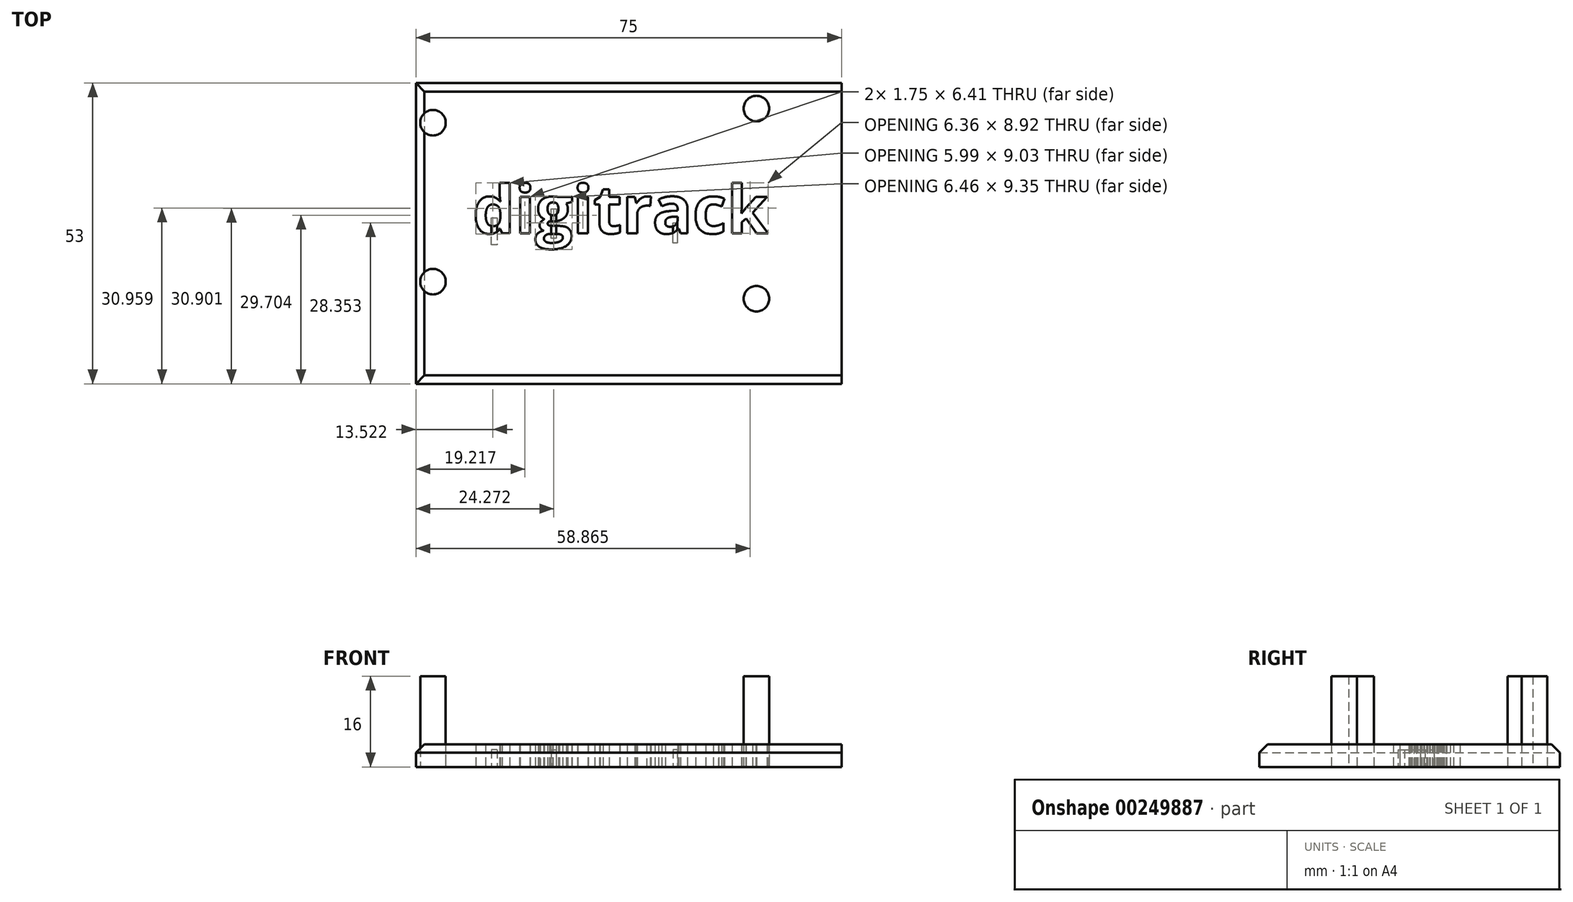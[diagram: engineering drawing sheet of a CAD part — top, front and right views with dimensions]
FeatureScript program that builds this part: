
annotation { "Feature Type Name" : "Feature", "Feature Type Description" : "" }
export const myFeature = defineFeature(function(context is Context, id is Id, definition is map)
    precondition{}
    {
        {
            var Q0;
            Q0=qCreatedBy(makeId("Top.planeOp"),FACE);
            var sketch = newSketch(context, id + "F0", { "sketchPlane" : qUnion([Q0])});
            skLineSegment(sketch, "E0.bottom", {"start": v(37.5, -26.5) * mm, "end": v(-37.5, -26.5) * mm});
            skLineSegment(sketch, "E0.top", {"start": v(37.5, 26.5) * mm, "end": v(-37.5, 26.5) * mm});
            skLineSegment(sketch, "E0.left", {"start": v(37.5, -26.5) * mm, "end": v(37.5, 26.5) * mm});
            skLineSegment(sketch, "E0.right", {"start": v(-37.5, -26.5) * mm, "end": v(-37.5, 26.5) * mm});
            skPoint(sketch, "E0.middle", {"position": v(0, 0) * mm});
            skSolve(sketch);
        }
        {
            var Q0;
            Q0 = qSketchRegion(id + "F0", true);
            extrude(context, id + "F1", {"entities" : qUnion([Q0]), "depth" : 4 * mm});
        }
        {
            var Q0;
            Q0=qCreatedBy(makeId("Top.planeOp"),FACE);
            var sketch = newSketch(context, id + "F2", { "sketchPlane" : qUnion([Q0])});
            skLineSegment(sketch, "E1", {"start": v(0, 0) * mm, "end": v(37.5, 0) * mm});
            skLineSegment(sketch, "E2", {"start": v(37.5, 0) * mm, "end": v(22.5, 0) * mm});
            skLineSegment(sketch, "E3", {"start": v(22.5, 0) * mm, "end": v(22.5, 22) * mm});
            skLineSegment(sketch, "E4", {"start": v(22.5, 0) * mm, "end": v(22.5, -26.5) * mm});
            skLineSegment(sketch, "E5", {"start": v(22.5, -26.5) * mm, "end": v(22.5, -11.5) * mm});
            skLineSegment(sketch, "E6", {"start": v(0, 0) * mm, "end": v(-37.5, 0) * mm});
            skLineSegment(sketch, "E7", {"start": v(-37.5, 0) * mm, "end": v(-34.5, 0) * mm});
            skLineSegment(sketch, "E8", {"start": v(-34.5, 0) * mm, "end": v(-34.5, 26.5) * mm});
            skLineSegment(sketch, "E9", {"start": v(-34.5, 26.5) * mm, "end": v(-34.5, 19.5) * mm});
            skLineSegment(sketch, "E10", {"start": v(-34.5, 0) * mm, "end": v(-34.5, -26.5) * mm});
            skLineSegment(sketch, "E11", {"start": v(-34.5, -26.5) * mm, "end": v(-34.5, -8.5) * mm});
            skCircle(sketch, "E12", {"center": v(-34.5, -8.5) * mm, "radius": 2.25 * mm});
            skCircle(sketch, "E13", {"center": v(-34.5, 19.5) * mm, "radius": 2.25 * mm});
            skCircle(sketch, "E14", {"center": v(22.5, 22) * mm, "radius": 2.25 * mm});
            skCircle(sketch, "E15", {"center": v(22.5, -11.5) * mm, "radius": 2.25 * mm});
            skSolve(sketch);
        }
        {
            var Q0;
            Q0 = qSketchRegion(id + "F2", true);
            extrude(context, id + "F3", {"entities" : qUnion([Q0]), "depth" : 16 * mm});
        }
        {
            var Q0;
            Q0=makeQuery(id+"F1.opExtrude","CAP_EDGE",EDGE,{"disambiguationData":[OSD([sQuery(id+"F0.wireOp",EDGE,"E0.right")])],"isStart":false});
            var Q1;
            Q1=makeQuery(id+"F1.opExtrude","CAP_EDGE",EDGE,{"disambiguationData":[OSD([sQuery(id+"F0.wireOp",EDGE,"E0.bottom")])],"isStart":false});
            var Q2;
            Q2=makeQuery(id+"F1.opExtrude","CAP_EDGE",EDGE,{"disambiguationData":[OSD([sQuery(id+"F0.wireOp",EDGE,"E0.top")])],"isStart":false});
            chamfer(context, id + "F4", {"entities" : qUnion([Q0, Q1, Q2]), "width" : 1.5 * mm, "tangentPropagation" : true});
        }
        {
            var Q0;
            Q0=qCreatedBy(makeId("Top.planeOp"),FACE);
            var sketch = newSketch(context, id + "F5", { "sketchPlane" : qUnion([Q0])});
            skText(sketch, "E16", { "text": "digitrack", "fontName": "OpenSans-Bold.ttf"});
            const initialGuessF5  = {"E16": [0, 0, 1, 0, 0.00845]};
            skSetInitialGuess(sketch, initialGuessF5);
            skSolve(sketch);
        }
        {
            var Q0;
            Q0 = qSketchRegion(id + "F5", true);
            extrude(context, id + "F6", {"entities" : qUnion([Q0]), "depth" : 8 * mm});
        }
        {
            var Q0;
            Q0=makeQuery(id+"F6.opExtrude","SWEPT_BODY",BODY,{"disambiguationData":[OSD([sQuery(id+"F5.wireOp",EDGE,"E16.sketch_text.stroke-0"),sQuery(id+"F5.wireOp",EDGE,"E16.sketch_text.stroke-1"),sQuery(id+"F5.wireOp",EDGE,"E16.sketch_text.stroke-2"),sQuery(id+"F5.wireOp",EDGE,"E16.sketch_text.stroke-3"),sQuery(id+"F5.wireOp",EDGE,"E16.sketch_text.stroke-4"),sQuery(id+"F5.wireOp",EDGE,"E16.sketch_text.stroke-5"),sQuery(id+"F5.wireOp",EDGE,"E16.sketch_text.stroke-6"),sQuery(id+"F5.wireOp",EDGE,"E16.sketch_text.stroke-7"),sQuery(id+"F5.wireOp",EDGE,"E16.sketch_text.stroke-8"),sQuery(id+"F5.wireOp",EDGE,"E16.sketch_text.stroke-9"),sQuery(id+"F5.wireOp",EDGE,"E16.sketch_text.stroke-10"),sQuery(id+"F5.wireOp",EDGE,"E16.sketch_text.stroke-11"),sQuery(id+"F5.wireOp",EDGE,"E16.sketch_text.stroke-12"),sQuery(id+"F5.wireOp",EDGE,"E16.sketch_text.stroke-13"),sQuery(id+"F5.wireOp",EDGE,"E16.sketch_text.stroke-14"),sQuery(id+"F5.wireOp",EDGE,"E16.sketch_text.stroke-15"),sQuery(id+"F5.wireOp",EDGE,"E16.sketch_text.stroke-16"),sQuery(id+"F5.wireOp",EDGE,"E16.sketch_text.stroke-17"),sQuery(id+"F5.wireOp",EDGE,"E16.sketch_text.stroke-18"),sQuery(id+"F5.wireOp",EDGE,"E16.sketch_text.stroke-19"),sQuery(id+"F5.wireOp",EDGE,"E16.sketch_text.stroke-20"),sQuery(id+"F5.wireOp",EDGE,"E16.sketch_text.stroke-21"),sQuery(id+"F5.wireOp",EDGE,"E16.sketch_text.stroke-22")])]});
            var Q1;
            Q1=makeQuery(id+"F6.opExtrude","SWEPT_BODY",BODY,{"disambiguationData":[OSD([sQuery(id+"F5.wireOp",EDGE,"E16.sketch_text.stroke-23"),sQuery(id+"F5.wireOp",EDGE,"E16.sketch_text.stroke-24"),sQuery(id+"F5.wireOp",EDGE,"E16.sketch_text.stroke-25"),sQuery(id+"F5.wireOp",EDGE,"E16.sketch_text.stroke-26"),sQuery(id+"F5.wireOp",EDGE,"E16.sketch_text.stroke-27")])]});
            var Q2;
            Q2=makeQuery(id+"F6.opExtrude","SWEPT_BODY",BODY,{"disambiguationData":[OSD([sQuery(id+"F5.wireOp",EDGE,"E16.sketch_text.stroke-28"),sQuery(id+"F5.wireOp",EDGE,"E16.sketch_text.stroke-29"),sQuery(id+"F5.wireOp",EDGE,"E16.sketch_text.stroke-30"),sQuery(id+"F5.wireOp",EDGE,"E16.sketch_text.stroke-31")])]});
            var Q3;
            Q3=makeQuery(id+"F6.opExtrude","SWEPT_BODY",BODY,{"disambiguationData":[OSD([sQuery(id+"F5.wireOp",EDGE,"E16.sketch_text.stroke-32"),sQuery(id+"F5.wireOp",EDGE,"E16.sketch_text.stroke-33"),sQuery(id+"F5.wireOp",EDGE,"E16.sketch_text.stroke-34"),sQuery(id+"F5.wireOp",EDGE,"E16.sketch_text.stroke-35"),sQuery(id+"F5.wireOp",EDGE,"E16.sketch_text.stroke-36"),sQuery(id+"F5.wireOp",EDGE,"E16.sketch_text.stroke-37"),sQuery(id+"F5.wireOp",EDGE,"E16.sketch_text.stroke-38"),sQuery(id+"F5.wireOp",EDGE,"E16.sketch_text.stroke-39"),sQuery(id+"F5.wireOp",EDGE,"E16.sketch_text.stroke-40"),sQuery(id+"F5.wireOp",EDGE,"E16.sketch_text.stroke-41"),sQuery(id+"F5.wireOp",EDGE,"E16.sketch_text.stroke-42"),sQuery(id+"F5.wireOp",EDGE,"E16.sketch_text.stroke-43"),sQuery(id+"F5.wireOp",EDGE,"E16.sketch_text.stroke-44"),sQuery(id+"F5.wireOp",EDGE,"E16.sketch_text.stroke-45"),sQuery(id+"F5.wireOp",EDGE,"E16.sketch_text.stroke-46"),sQuery(id+"F5.wireOp",EDGE,"E16.sketch_text.stroke-47"),sQuery(id+"F5.wireOp",EDGE,"E16.sketch_text.stroke-48"),sQuery(id+"F5.wireOp",EDGE,"E16.sketch_text.stroke-49"),sQuery(id+"F5.wireOp",EDGE,"E16.sketch_text.stroke-50"),sQuery(id+"F5.wireOp",EDGE,"E16.sketch_text.stroke-51"),sQuery(id+"F5.wireOp",EDGE,"E16.sketch_text.stroke-52"),sQuery(id+"F5.wireOp",EDGE,"E16.sketch_text.stroke-53"),sQuery(id+"F5.wireOp",EDGE,"E16.sketch_text.stroke-54"),sQuery(id+"F5.wireOp",EDGE,"E16.sketch_text.stroke-55"),sQuery(id+"F5.wireOp",EDGE,"E16.sketch_text.stroke-56"),sQuery(id+"F5.wireOp",EDGE,"E16.sketch_text.stroke-57"),sQuery(id+"F5.wireOp",EDGE,"E16.sketch_text.stroke-58"),sQuery(id+"F5.wireOp",EDGE,"E16.sketch_text.stroke-59"),sQuery(id+"F5.wireOp",EDGE,"E16.sketch_text.stroke-60"),sQuery(id+"F5.wireOp",EDGE,"E16.sketch_text.stroke-61"),sQuery(id+"F5.wireOp",EDGE,"E16.sketch_text.stroke-62"),sQuery(id+"F5.wireOp",EDGE,"E16.sketch_text.stroke-63"),sQuery(id+"F5.wireOp",EDGE,"E16.sketch_text.stroke-64"),sQuery(id+"F5.wireOp",EDGE,"E16.sketch_text.stroke-65"),sQuery(id+"F5.wireOp",EDGE,"E16.sketch_text.stroke-66"),sQuery(id+"F5.wireOp",EDGE,"E16.sketch_text.stroke-67"),sQuery(id+"F5.wireOp",EDGE,"E16.sketch_text.stroke-68"),sQuery(id+"F5.wireOp",EDGE,"E16.sketch_text.stroke-69"),sQuery(id+"F5.wireOp",EDGE,"E16.sketch_text.stroke-70"),sQuery(id+"F5.wireOp",EDGE,"E16.sketch_text.stroke-71"),sQuery(id+"F5.wireOp",EDGE,"E16.sketch_text.stroke-72"),sQuery(id+"F5.wireOp",EDGE,"E16.sketch_text.stroke-73"),sQuery(id+"F5.wireOp",EDGE,"E16.sketch_text.stroke-74"),sQuery(id+"F5.wireOp",EDGE,"E16.sketch_text.stroke-75")])]});
            var Q4;
            Q4=makeQuery(id+"F6.opExtrude","SWEPT_BODY",BODY,{"disambiguationData":[OSD([sQuery(id+"F5.wireOp",EDGE,"E16.sketch_text.stroke-76"),sQuery(id+"F5.wireOp",EDGE,"E16.sketch_text.stroke-77"),sQuery(id+"F5.wireOp",EDGE,"E16.sketch_text.stroke-78"),sQuery(id+"F5.wireOp",EDGE,"E16.sketch_text.stroke-79"),sQuery(id+"F5.wireOp",EDGE,"E16.sketch_text.stroke-80")])]});
            var Q5;
            Q5=makeQuery(id+"F6.opExtrude","SWEPT_BODY",BODY,{"disambiguationData":[OSD([sQuery(id+"F5.wireOp",EDGE,"E16.sketch_text.stroke-81"),sQuery(id+"F5.wireOp",EDGE,"E16.sketch_text.stroke-82"),sQuery(id+"F5.wireOp",EDGE,"E16.sketch_text.stroke-83"),sQuery(id+"F5.wireOp",EDGE,"E16.sketch_text.stroke-84")])]});
            var Q6;
            Q6=makeQuery(id+"F6.opExtrude","SWEPT_BODY",BODY,{"disambiguationData":[OSD([sQuery(id+"F5.wireOp",EDGE,"E16.sketch_text.stroke-85"),sQuery(id+"F5.wireOp",EDGE,"E16.sketch_text.stroke-86"),sQuery(id+"F5.wireOp",EDGE,"E16.sketch_text.stroke-87"),sQuery(id+"F5.wireOp",EDGE,"E16.sketch_text.stroke-88"),sQuery(id+"F5.wireOp",EDGE,"E16.sketch_text.stroke-89"),sQuery(id+"F5.wireOp",EDGE,"E16.sketch_text.stroke-90"),sQuery(id+"F5.wireOp",EDGE,"E16.sketch_text.stroke-91"),sQuery(id+"F5.wireOp",EDGE,"E16.sketch_text.stroke-92"),sQuery(id+"F5.wireOp",EDGE,"E16.sketch_text.stroke-93"),sQuery(id+"F5.wireOp",EDGE,"E16.sketch_text.stroke-94"),sQuery(id+"F5.wireOp",EDGE,"E16.sketch_text.stroke-95"),sQuery(id+"F5.wireOp",EDGE,"E16.sketch_text.stroke-96"),sQuery(id+"F5.wireOp",EDGE,"E16.sketch_text.stroke-97"),sQuery(id+"F5.wireOp",EDGE,"E16.sketch_text.stroke-98"),sQuery(id+"F5.wireOp",EDGE,"E16.sketch_text.stroke-99"),sQuery(id+"F5.wireOp",EDGE,"E16.sketch_text.stroke-100"),sQuery(id+"F5.wireOp",EDGE,"E16.sketch_text.stroke-101"),sQuery(id+"F5.wireOp",EDGE,"E16.sketch_text.stroke-102")])]});
            var Q7;
            Q7=makeQuery(id+"F6.opExtrude","SWEPT_BODY",BODY,{"disambiguationData":[OSD([sQuery(id+"F5.wireOp",EDGE,"E16.sketch_text.stroke-103"),sQuery(id+"F5.wireOp",EDGE,"E16.sketch_text.stroke-104"),sQuery(id+"F5.wireOp",EDGE,"E16.sketch_text.stroke-105"),sQuery(id+"F5.wireOp",EDGE,"E16.sketch_text.stroke-106"),sQuery(id+"F5.wireOp",EDGE,"E16.sketch_text.stroke-107"),sQuery(id+"F5.wireOp",EDGE,"E16.sketch_text.stroke-108"),sQuery(id+"F5.wireOp",EDGE,"E16.sketch_text.stroke-109"),sQuery(id+"F5.wireOp",EDGE,"E16.sketch_text.stroke-110"),sQuery(id+"F5.wireOp",EDGE,"E16.sketch_text.stroke-111"),sQuery(id+"F5.wireOp",EDGE,"E16.sketch_text.stroke-112"),sQuery(id+"F5.wireOp",EDGE,"E16.sketch_text.stroke-113"),sQuery(id+"F5.wireOp",EDGE,"E16.sketch_text.stroke-114"),sQuery(id+"F5.wireOp",EDGE,"E16.sketch_text.stroke-115")])]});
            var Q8;
            Q8=makeQuery(id+"F6.opExtrude","SWEPT_BODY",BODY,{"disambiguationData":[OSD([sQuery(id+"F5.wireOp",EDGE,"E16.sketch_text.stroke-116"),sQuery(id+"F5.wireOp",EDGE,"E16.sketch_text.stroke-117"),sQuery(id+"F5.wireOp",EDGE,"E16.sketch_text.stroke-118"),sQuery(id+"F5.wireOp",EDGE,"E16.sketch_text.stroke-119"),sQuery(id+"F5.wireOp",EDGE,"E16.sketch_text.stroke-120"),sQuery(id+"F5.wireOp",EDGE,"E16.sketch_text.stroke-121"),sQuery(id+"F5.wireOp",EDGE,"E16.sketch_text.stroke-122"),sQuery(id+"F5.wireOp",EDGE,"E16.sketch_text.stroke-123"),sQuery(id+"F5.wireOp",EDGE,"E16.sketch_text.stroke-124"),sQuery(id+"F5.wireOp",EDGE,"E16.sketch_text.stroke-125"),sQuery(id+"F5.wireOp",EDGE,"E16.sketch_text.stroke-126"),sQuery(id+"F5.wireOp",EDGE,"E16.sketch_text.stroke-127"),sQuery(id+"F5.wireOp",EDGE,"E16.sketch_text.stroke-128"),sQuery(id+"F5.wireOp",EDGE,"E16.sketch_text.stroke-129"),sQuery(id+"F5.wireOp",EDGE,"E16.sketch_text.stroke-130"),sQuery(id+"F5.wireOp",EDGE,"E16.sketch_text.stroke-131"),sQuery(id+"F5.wireOp",EDGE,"E16.sketch_text.stroke-132"),sQuery(id+"F5.wireOp",EDGE,"E16.sketch_text.stroke-133"),sQuery(id+"F5.wireOp",EDGE,"E16.sketch_text.stroke-134"),sQuery(id+"F5.wireOp",EDGE,"E16.sketch_text.stroke-135"),sQuery(id+"F5.wireOp",EDGE,"E16.sketch_text.stroke-136"),sQuery(id+"F5.wireOp",EDGE,"E16.sketch_text.stroke-137"),sQuery(id+"F5.wireOp",EDGE,"E16.sketch_text.stroke-138"),sQuery(id+"F5.wireOp",EDGE,"E16.sketch_text.stroke-139"),sQuery(id+"F5.wireOp",EDGE,"E16.sketch_text.stroke-140")])]});
            var Q9;
            Q9=makeQuery(id+"F6.opExtrude","SWEPT_BODY",BODY,{"disambiguationData":[OSD([sQuery(id+"F5.wireOp",EDGE,"E16.sketch_text.stroke-141"),sQuery(id+"F5.wireOp",EDGE,"E16.sketch_text.stroke-142"),sQuery(id+"F5.wireOp",EDGE,"E16.sketch_text.stroke-143"),sQuery(id+"F5.wireOp",EDGE,"E16.sketch_text.stroke-144"),sQuery(id+"F5.wireOp",EDGE,"E16.sketch_text.stroke-145"),sQuery(id+"F5.wireOp",EDGE,"E16.sketch_text.stroke-146"),sQuery(id+"F5.wireOp",EDGE,"E16.sketch_text.stroke-147"),sQuery(id+"F5.wireOp",EDGE,"E16.sketch_text.stroke-148"),sQuery(id+"F5.wireOp",EDGE,"E16.sketch_text.stroke-149"),sQuery(id+"F5.wireOp",EDGE,"E16.sketch_text.stroke-150"),sQuery(id+"F5.wireOp",EDGE,"E16.sketch_text.stroke-151"),sQuery(id+"F5.wireOp",EDGE,"E16.sketch_text.stroke-152"),sQuery(id+"F5.wireOp",EDGE,"E16.sketch_text.stroke-153"),sQuery(id+"F5.wireOp",EDGE,"E16.sketch_text.stroke-154")])]});
            var Q10;
            Q10=makeQuery(id+"F6.opExtrude","SWEPT_BODY",BODY,{"disambiguationData":[OSD([sQuery(id+"F5.wireOp",EDGE,"E16.sketch_text.stroke-155"),sQuery(id+"F5.wireOp",EDGE,"E16.sketch_text.stroke-156"),sQuery(id+"F5.wireOp",EDGE,"E16.sketch_text.stroke-157"),sQuery(id+"F5.wireOp",EDGE,"E16.sketch_text.stroke-158"),sQuery(id+"F5.wireOp",EDGE,"E16.sketch_text.stroke-159"),sQuery(id+"F5.wireOp",EDGE,"E16.sketch_text.stroke-160"),sQuery(id+"F5.wireOp",EDGE,"E16.sketch_text.stroke-161"),sQuery(id+"F5.wireOp",EDGE,"E16.sketch_text.stroke-162"),sQuery(id+"F5.wireOp",EDGE,"E16.sketch_text.stroke-163"),sQuery(id+"F5.wireOp",EDGE,"E16.sketch_text.stroke-164"),sQuery(id+"F5.wireOp",EDGE,"E16.sketch_text.stroke-165"),sQuery(id+"F5.wireOp",EDGE,"E16.sketch_text.stroke-166"),sQuery(id+"F5.wireOp",EDGE,"E16.sketch_text.stroke-167"),sQuery(id+"F5.wireOp",EDGE,"E16.sketch_text.stroke-168"),sQuery(id+"F5.wireOp",EDGE,"E16.sketch_text.stroke-169")])]});
            transform(context, id + "F7", {"entities" : qUnion([Q0, Q1, Q2, Q3, Q4, Q5, Q6, Q7, Q8, Q9, Q10]), "transformType" : TransformType.TRANSLATION_3D, "dx" : -27.5 * mm, "dy" : 0 * mm, "dz" : 0 * mm, "makeCopy" : false});
        }
        {
            var Q0;
            Q0=makeQuery(id+"F6.opExtrude","SWEPT_BODY",BODY,{"disambiguationData":[OSD([sQuery(id+"F5.wireOp",EDGE,"E16.sketch_text.stroke-155"),sQuery(id+"F5.wireOp",EDGE,"E16.sketch_text.stroke-156"),sQuery(id+"F5.wireOp",EDGE,"E16.sketch_text.stroke-157"),sQuery(id+"F5.wireOp",EDGE,"E16.sketch_text.stroke-158"),sQuery(id+"F5.wireOp",EDGE,"E16.sketch_text.stroke-159"),sQuery(id+"F5.wireOp",EDGE,"E16.sketch_text.stroke-160"),sQuery(id+"F5.wireOp",EDGE,"E16.sketch_text.stroke-161"),sQuery(id+"F5.wireOp",EDGE,"E16.sketch_text.stroke-162"),sQuery(id+"F5.wireOp",EDGE,"E16.sketch_text.stroke-163"),sQuery(id+"F5.wireOp",EDGE,"E16.sketch_text.stroke-164"),sQuery(id+"F5.wireOp",EDGE,"E16.sketch_text.stroke-165"),sQuery(id+"F5.wireOp",EDGE,"E16.sketch_text.stroke-166"),sQuery(id+"F5.wireOp",EDGE,"E16.sketch_text.stroke-167"),sQuery(id+"F5.wireOp",EDGE,"E16.sketch_text.stroke-168"),sQuery(id+"F5.wireOp",EDGE,"E16.sketch_text.stroke-169")])]});
            var Q1;
            Q1=makeQuery(id+"F6.opExtrude","SWEPT_BODY",BODY,{"disambiguationData":[OSD([sQuery(id+"F5.wireOp",EDGE,"E16.sketch_text.stroke-141"),sQuery(id+"F5.wireOp",EDGE,"E16.sketch_text.stroke-142"),sQuery(id+"F5.wireOp",EDGE,"E16.sketch_text.stroke-143"),sQuery(id+"F5.wireOp",EDGE,"E16.sketch_text.stroke-144"),sQuery(id+"F5.wireOp",EDGE,"E16.sketch_text.stroke-145"),sQuery(id+"F5.wireOp",EDGE,"E16.sketch_text.stroke-146"),sQuery(id+"F5.wireOp",EDGE,"E16.sketch_text.stroke-147"),sQuery(id+"F5.wireOp",EDGE,"E16.sketch_text.stroke-148"),sQuery(id+"F5.wireOp",EDGE,"E16.sketch_text.stroke-149"),sQuery(id+"F5.wireOp",EDGE,"E16.sketch_text.stroke-150"),sQuery(id+"F5.wireOp",EDGE,"E16.sketch_text.stroke-151"),sQuery(id+"F5.wireOp",EDGE,"E16.sketch_text.stroke-152"),sQuery(id+"F5.wireOp",EDGE,"E16.sketch_text.stroke-153"),sQuery(id+"F5.wireOp",EDGE,"E16.sketch_text.stroke-154")])]});
            var Q2;
            Q2=makeQuery(id+"F6.opExtrude","SWEPT_BODY",BODY,{"disambiguationData":[OSD([sQuery(id+"F5.wireOp",EDGE,"E16.sketch_text.stroke-116"),sQuery(id+"F5.wireOp",EDGE,"E16.sketch_text.stroke-117"),sQuery(id+"F5.wireOp",EDGE,"E16.sketch_text.stroke-118"),sQuery(id+"F5.wireOp",EDGE,"E16.sketch_text.stroke-119"),sQuery(id+"F5.wireOp",EDGE,"E16.sketch_text.stroke-120"),sQuery(id+"F5.wireOp",EDGE,"E16.sketch_text.stroke-121"),sQuery(id+"F5.wireOp",EDGE,"E16.sketch_text.stroke-122"),sQuery(id+"F5.wireOp",EDGE,"E16.sketch_text.stroke-123"),sQuery(id+"F5.wireOp",EDGE,"E16.sketch_text.stroke-124"),sQuery(id+"F5.wireOp",EDGE,"E16.sketch_text.stroke-125"),sQuery(id+"F5.wireOp",EDGE,"E16.sketch_text.stroke-126"),sQuery(id+"F5.wireOp",EDGE,"E16.sketch_text.stroke-127"),sQuery(id+"F5.wireOp",EDGE,"E16.sketch_text.stroke-128"),sQuery(id+"F5.wireOp",EDGE,"E16.sketch_text.stroke-129"),sQuery(id+"F5.wireOp",EDGE,"E16.sketch_text.stroke-130"),sQuery(id+"F5.wireOp",EDGE,"E16.sketch_text.stroke-131"),sQuery(id+"F5.wireOp",EDGE,"E16.sketch_text.stroke-132"),sQuery(id+"F5.wireOp",EDGE,"E16.sketch_text.stroke-133"),sQuery(id+"F5.wireOp",EDGE,"E16.sketch_text.stroke-134"),sQuery(id+"F5.wireOp",EDGE,"E16.sketch_text.stroke-135"),sQuery(id+"F5.wireOp",EDGE,"E16.sketch_text.stroke-136"),sQuery(id+"F5.wireOp",EDGE,"E16.sketch_text.stroke-137"),sQuery(id+"F5.wireOp",EDGE,"E16.sketch_text.stroke-138"),sQuery(id+"F5.wireOp",EDGE,"E16.sketch_text.stroke-139"),sQuery(id+"F5.wireOp",EDGE,"E16.sketch_text.stroke-140")])]});
            var Q3;
            Q3=makeQuery(id+"F6.opExtrude","SWEPT_BODY",BODY,{"disambiguationData":[OSD([sQuery(id+"F5.wireOp",EDGE,"E16.sketch_text.stroke-103"),sQuery(id+"F5.wireOp",EDGE,"E16.sketch_text.stroke-104"),sQuery(id+"F5.wireOp",EDGE,"E16.sketch_text.stroke-105"),sQuery(id+"F5.wireOp",EDGE,"E16.sketch_text.stroke-106"),sQuery(id+"F5.wireOp",EDGE,"E16.sketch_text.stroke-107"),sQuery(id+"F5.wireOp",EDGE,"E16.sketch_text.stroke-108"),sQuery(id+"F5.wireOp",EDGE,"E16.sketch_text.stroke-109"),sQuery(id+"F5.wireOp",EDGE,"E16.sketch_text.stroke-110"),sQuery(id+"F5.wireOp",EDGE,"E16.sketch_text.stroke-111"),sQuery(id+"F5.wireOp",EDGE,"E16.sketch_text.stroke-112"),sQuery(id+"F5.wireOp",EDGE,"E16.sketch_text.stroke-113"),sQuery(id+"F5.wireOp",EDGE,"E16.sketch_text.stroke-114"),sQuery(id+"F5.wireOp",EDGE,"E16.sketch_text.stroke-115")])]});
            var Q4;
            Q4=makeQuery(id+"F6.opExtrude","SWEPT_BODY",BODY,{"disambiguationData":[OSD([sQuery(id+"F5.wireOp",EDGE,"E16.sketch_text.stroke-85"),sQuery(id+"F5.wireOp",EDGE,"E16.sketch_text.stroke-86"),sQuery(id+"F5.wireOp",EDGE,"E16.sketch_text.stroke-87"),sQuery(id+"F5.wireOp",EDGE,"E16.sketch_text.stroke-88"),sQuery(id+"F5.wireOp",EDGE,"E16.sketch_text.stroke-89"),sQuery(id+"F5.wireOp",EDGE,"E16.sketch_text.stroke-90"),sQuery(id+"F5.wireOp",EDGE,"E16.sketch_text.stroke-91"),sQuery(id+"F5.wireOp",EDGE,"E16.sketch_text.stroke-92"),sQuery(id+"F5.wireOp",EDGE,"E16.sketch_text.stroke-93"),sQuery(id+"F5.wireOp",EDGE,"E16.sketch_text.stroke-94"),sQuery(id+"F5.wireOp",EDGE,"E16.sketch_text.stroke-95"),sQuery(id+"F5.wireOp",EDGE,"E16.sketch_text.stroke-96"),sQuery(id+"F5.wireOp",EDGE,"E16.sketch_text.stroke-97"),sQuery(id+"F5.wireOp",EDGE,"E16.sketch_text.stroke-98"),sQuery(id+"F5.wireOp",EDGE,"E16.sketch_text.stroke-99"),sQuery(id+"F5.wireOp",EDGE,"E16.sketch_text.stroke-100"),sQuery(id+"F5.wireOp",EDGE,"E16.sketch_text.stroke-101"),sQuery(id+"F5.wireOp",EDGE,"E16.sketch_text.stroke-102")])]});
            var Q5;
            Q5=makeQuery(id+"F6.opExtrude","SWEPT_BODY",BODY,{"disambiguationData":[OSD([sQuery(id+"F5.wireOp",EDGE,"E16.sketch_text.stroke-81"),sQuery(id+"F5.wireOp",EDGE,"E16.sketch_text.stroke-82"),sQuery(id+"F5.wireOp",EDGE,"E16.sketch_text.stroke-83"),sQuery(id+"F5.wireOp",EDGE,"E16.sketch_text.stroke-84")])]});
            var Q6;
            Q6=makeQuery(id+"F6.opExtrude","SWEPT_BODY",BODY,{"disambiguationData":[OSD([sQuery(id+"F5.wireOp",EDGE,"E16.sketch_text.stroke-76"),sQuery(id+"F5.wireOp",EDGE,"E16.sketch_text.stroke-77"),sQuery(id+"F5.wireOp",EDGE,"E16.sketch_text.stroke-78"),sQuery(id+"F5.wireOp",EDGE,"E16.sketch_text.stroke-79"),sQuery(id+"F5.wireOp",EDGE,"E16.sketch_text.stroke-80")])]});
            var Q7;
            Q7=makeQuery(id+"F6.opExtrude","SWEPT_BODY",BODY,{"disambiguationData":[OSD([sQuery(id+"F5.wireOp",EDGE,"E16.sketch_text.stroke-32"),sQuery(id+"F5.wireOp",EDGE,"E16.sketch_text.stroke-33"),sQuery(id+"F5.wireOp",EDGE,"E16.sketch_text.stroke-34"),sQuery(id+"F5.wireOp",EDGE,"E16.sketch_text.stroke-35"),sQuery(id+"F5.wireOp",EDGE,"E16.sketch_text.stroke-36"),sQuery(id+"F5.wireOp",EDGE,"E16.sketch_text.stroke-37"),sQuery(id+"F5.wireOp",EDGE,"E16.sketch_text.stroke-38"),sQuery(id+"F5.wireOp",EDGE,"E16.sketch_text.stroke-39"),sQuery(id+"F5.wireOp",EDGE,"E16.sketch_text.stroke-40"),sQuery(id+"F5.wireOp",EDGE,"E16.sketch_text.stroke-41"),sQuery(id+"F5.wireOp",EDGE,"E16.sketch_text.stroke-42"),sQuery(id+"F5.wireOp",EDGE,"E16.sketch_text.stroke-43"),sQuery(id+"F5.wireOp",EDGE,"E16.sketch_text.stroke-44"),sQuery(id+"F5.wireOp",EDGE,"E16.sketch_text.stroke-45"),sQuery(id+"F5.wireOp",EDGE,"E16.sketch_text.stroke-46"),sQuery(id+"F5.wireOp",EDGE,"E16.sketch_text.stroke-47"),sQuery(id+"F5.wireOp",EDGE,"E16.sketch_text.stroke-48"),sQuery(id+"F5.wireOp",EDGE,"E16.sketch_text.stroke-49"),sQuery(id+"F5.wireOp",EDGE,"E16.sketch_text.stroke-50"),sQuery(id+"F5.wireOp",EDGE,"E16.sketch_text.stroke-51"),sQuery(id+"F5.wireOp",EDGE,"E16.sketch_text.stroke-52"),sQuery(id+"F5.wireOp",EDGE,"E16.sketch_text.stroke-53"),sQuery(id+"F5.wireOp",EDGE,"E16.sketch_text.stroke-54"),sQuery(id+"F5.wireOp",EDGE,"E16.sketch_text.stroke-55"),sQuery(id+"F5.wireOp",EDGE,"E16.sketch_text.stroke-56"),sQuery(id+"F5.wireOp",EDGE,"E16.sketch_text.stroke-57"),sQuery(id+"F5.wireOp",EDGE,"E16.sketch_text.stroke-58"),sQuery(id+"F5.wireOp",EDGE,"E16.sketch_text.stroke-59"),sQuery(id+"F5.wireOp",EDGE,"E16.sketch_text.stroke-60"),sQuery(id+"F5.wireOp",EDGE,"E16.sketch_text.stroke-61"),sQuery(id+"F5.wireOp",EDGE,"E16.sketch_text.stroke-62"),sQuery(id+"F5.wireOp",EDGE,"E16.sketch_text.stroke-63"),sQuery(id+"F5.wireOp",EDGE,"E16.sketch_text.stroke-64"),sQuery(id+"F5.wireOp",EDGE,"E16.sketch_text.stroke-65"),sQuery(id+"F5.wireOp",EDGE,"E16.sketch_text.stroke-66"),sQuery(id+"F5.wireOp",EDGE,"E16.sketch_text.stroke-67"),sQuery(id+"F5.wireOp",EDGE,"E16.sketch_text.stroke-68"),sQuery(id+"F5.wireOp",EDGE,"E16.sketch_text.stroke-69"),sQuery(id+"F5.wireOp",EDGE,"E16.sketch_text.stroke-70"),sQuery(id+"F5.wireOp",EDGE,"E16.sketch_text.stroke-71"),sQuery(id+"F5.wireOp",EDGE,"E16.sketch_text.stroke-72"),sQuery(id+"F5.wireOp",EDGE,"E16.sketch_text.stroke-73"),sQuery(id+"F5.wireOp",EDGE,"E16.sketch_text.stroke-74"),sQuery(id+"F5.wireOp",EDGE,"E16.sketch_text.stroke-75")])]});
            var Q8;
            Q8=makeQuery(id+"F6.opExtrude","SWEPT_BODY",BODY,{"disambiguationData":[OSD([sQuery(id+"F5.wireOp",EDGE,"E16.sketch_text.stroke-28"),sQuery(id+"F5.wireOp",EDGE,"E16.sketch_text.stroke-29"),sQuery(id+"F5.wireOp",EDGE,"E16.sketch_text.stroke-30"),sQuery(id+"F5.wireOp",EDGE,"E16.sketch_text.stroke-31")])]});
            var Q9;
            Q9=makeQuery(id+"F6.opExtrude","SWEPT_BODY",BODY,{"disambiguationData":[OSD([sQuery(id+"F5.wireOp",EDGE,"E16.sketch_text.stroke-23"),sQuery(id+"F5.wireOp",EDGE,"E16.sketch_text.stroke-24"),sQuery(id+"F5.wireOp",EDGE,"E16.sketch_text.stroke-25"),sQuery(id+"F5.wireOp",EDGE,"E16.sketch_text.stroke-26"),sQuery(id+"F5.wireOp",EDGE,"E16.sketch_text.stroke-27")])]});
            var Q10;
            Q10=makeQuery(id+"F6.opExtrude","SWEPT_BODY",BODY,{"disambiguationData":[OSD([sQuery(id+"F5.wireOp",EDGE,"E16.sketch_text.stroke-0"),sQuery(id+"F5.wireOp",EDGE,"E16.sketch_text.stroke-1"),sQuery(id+"F5.wireOp",EDGE,"E16.sketch_text.stroke-2"),sQuery(id+"F5.wireOp",EDGE,"E16.sketch_text.stroke-3"),sQuery(id+"F5.wireOp",EDGE,"E16.sketch_text.stroke-4"),sQuery(id+"F5.wireOp",EDGE,"E16.sketch_text.stroke-5"),sQuery(id+"F5.wireOp",EDGE,"E16.sketch_text.stroke-6"),sQuery(id+"F5.wireOp",EDGE,"E16.sketch_text.stroke-7"),sQuery(id+"F5.wireOp",EDGE,"E16.sketch_text.stroke-8"),sQuery(id+"F5.wireOp",EDGE,"E16.sketch_text.stroke-9"),sQuery(id+"F5.wireOp",EDGE,"E16.sketch_text.stroke-10"),sQuery(id+"F5.wireOp",EDGE,"E16.sketch_text.stroke-11"),sQuery(id+"F5.wireOp",EDGE,"E16.sketch_text.stroke-12"),sQuery(id+"F5.wireOp",EDGE,"E16.sketch_text.stroke-13"),sQuery(id+"F5.wireOp",EDGE,"E16.sketch_text.stroke-14"),sQuery(id+"F5.wireOp",EDGE,"E16.sketch_text.stroke-15"),sQuery(id+"F5.wireOp",EDGE,"E16.sketch_text.stroke-16"),sQuery(id+"F5.wireOp",EDGE,"E16.sketch_text.stroke-17"),sQuery(id+"F5.wireOp",EDGE,"E16.sketch_text.stroke-18"),sQuery(id+"F5.wireOp",EDGE,"E16.sketch_text.stroke-19"),sQuery(id+"F5.wireOp",EDGE,"E16.sketch_text.stroke-20"),sQuery(id+"F5.wireOp",EDGE,"E16.sketch_text.stroke-21"),sQuery(id+"F5.wireOp",EDGE,"E16.sketch_text.stroke-22")])]});
            var Q11;
            Q11=makeQuery(id+"F1.opExtrude","SWEPT_BODY",BODY,{"disambiguationData":[OSD([sQuery(id+"F0.wireOp",EDGE,"E0.bottom"),sQuery(id+"F0.wireOp",EDGE,"E0.top"),sQuery(id+"F0.wireOp",EDGE,"E0.left"),sQuery(id+"F0.wireOp",EDGE,"E0.right")])]});
            booleanBodies(context, id + "F8", {"operationType" : BooleanOperationType.SUBTRACTION, "tools" : qUnion([Q0, Q1, Q2, Q3, Q4, Q5, Q6, Q7, Q8, Q9, Q10]), "targets" : qUnion([Q11])});
        }
        {
            var Q0;
            Q0=qCreatedBy(makeId("Top.planeOp"),FACE);
            var sketch = newSketch(context, id + "F9", { "sketchPlane" : qUnion([Q0])});
            skLineSegment(sketch, "E17", {"start": v(0, 0) * mm, "end": v(-13.69, 0) * mm});
            skLineSegment(sketch, "E18", {"start": v(-13.69, 0) * mm, "end": v(-13.69, 4.32) * mm});
            skLineSegment(sketch, "E19", {"start": v(-13.69, 4.32) * mm, "end": v(-12.81, 4.32) * mm});
            skLineSegment(sketch, "E20", {"start": v(-12.81, 4.32) * mm, "end": v(-12.81, -0.88) * mm});
            skLineSegment(sketch, "E21", {"start": v(-12.81, -0.88) * mm, "end": v(-13.69, -0.88) * mm});
            skLineSegment(sketch, "E22", {"start": v(-13.69, -0.88) * mm, "end": v(-13.69, 0) * mm});
            skLineSegment(sketch, "E23", {"start": v(-13.69, 0) * mm, "end": v(-24.22, 0) * mm});
            skLineSegment(sketch, "E24", {"start": v(-24.22, 0) * mm, "end": v(-24.22, 2.77) * mm});
            skLineSegment(sketch, "E25", {"start": v(-24.22, 2.77) * mm, "end": v(-23.22, 2.77) * mm});
            skLineSegment(sketch, "E26", {"start": v(-23.22, 2.77) * mm, "end": v(-23.22, -2.03) * mm});
            skLineSegment(sketch, "E27", {"start": v(-23.22, -2.03) * mm, "end": v(-24.22, -2.03) * mm});
            skLineSegment(sketch, "E28", {"start": v(-24.22, -2.03) * mm, "end": v(-24.22, 0) * mm});
            skLineSegment(sketch, "E29", {"start": v(0, 0) * mm, "end": v(7.81, 0) * mm});
            skLineSegment(sketch, "E30", {"start": v(7.81, 0) * mm, "end": v(7.81, 1.88) * mm});
            skLineSegment(sketch, "E31", {"start": v(7.81, 1.88) * mm, "end": v(8.56, 1.88) * mm});
            skLineSegment(sketch, "E32", {"start": v(8.56, 1.88) * mm, "end": v(8.56, -1.7) * mm});
            skLineSegment(sketch, "E33", {"start": v(8.56, -1.7) * mm, "end": v(7.81, -1.7) * mm});
            skLineSegment(sketch, "E34", {"start": v(7.81, -1.7) * mm, "end": v(7.81, 0) * mm});
            skSolve(sketch);
        }
        {
            var Q0;
            Q0 = qSketchRegion(id + "F9", true);
            extrude(context, id + "F10", {"entities" : qUnion([Q0]), "depth" : 3 * mm});
        }
    });
